# Revit family: NU-540(E)_230V Class II Type A2 BSC
name_source: partatom
category: Mechanical Equipment
revit_build: Autodesk Revit 2018 (Build: 20180423_1000(x64)
units: mm (PartAtom-declared; Revit-internal decimal feet)

## family parameters
Always vertical = Yes
Cut with Voids When Loaded = No
OmniClass Number = 23.75.00.00
OmniClass Title = Climate Control (HVAC)
Part Type = Normal
Room Calculation Point = No
Round Connector Dimension = Use Diameter
Shared = No
Work Plane-Based = No

## types (4) — shared parameters
Cabinet Height = 4' - 10 7/8"
Description = 230V Class II, Type A2 Biological Safety Cabinet
Manufacturer = NuAire Inc.
transition depth = 1' - 7 1/8"

## per-type parameters (varying)
| type | Cabinet Depth | Cabinet Width | Exhaust Center | Exhaust Diameter | Exhaust Filter Width | Overall Width | Workzone Width | crossbar | exhaust door width | exhaust ring inner | transition width | window width |
| NU-540-600(E) | 2' - 7 1/16" | 5' - 10 9/16" | 2' - 0" | 0' - 10" | 2' - 10 1/2" | 6' - 5 9/16" | 5' - 10 3/8" | 5' - 10 5/32" | 2' - 7 3/16" | 0' - 4 15/16" | 2' - 11 3/8" | 5' - 11 7/8" |
| NU-540-500(E) | 2' - 6" | 4' - 10 9/16" | 1' - 9" | 0' - 10" | 2' - 4 1/2" | 5' - 5 9/16" | 4' - 10 3/8" | 4' - 10 5/32" | 2' - 7 3/16" | 0' - 4 15/16" | 2' - 5 3/8" | 4' - 11 7/8" |
| NU-540-400(E) | 2' - 7 7/16" | 3' - 10 9/16" | 1' - 5" | 0' - 10" | 1' - 8 1/2" | 4' - 5 9/16" | 3' - 10 3/8" | 3' - 10 5/32" | 1' - 7 3/16" | 0' - 4 15/16" | 1' - 9 3/8" | 3' - 11 3/8" |
| NU-540-300(E) | 2' - 6" | 2' - 10 9/16" | 1' - 1" | 0' - 8" | 1' - 0 1/2" | 3' - 5 9/16" | 2' - 10 3/8" | 2' - 10 5/32" | 1' - 1 3/16" | 0' - 3 15/16" | 1' - 1 3/8" | 2' - 11 7/8" |

note: column(s) folded — value = type name in every type: Model

## geometry (parser evidence)
native form markers: Sweep x4
no freeform markers — native parametric forms only
